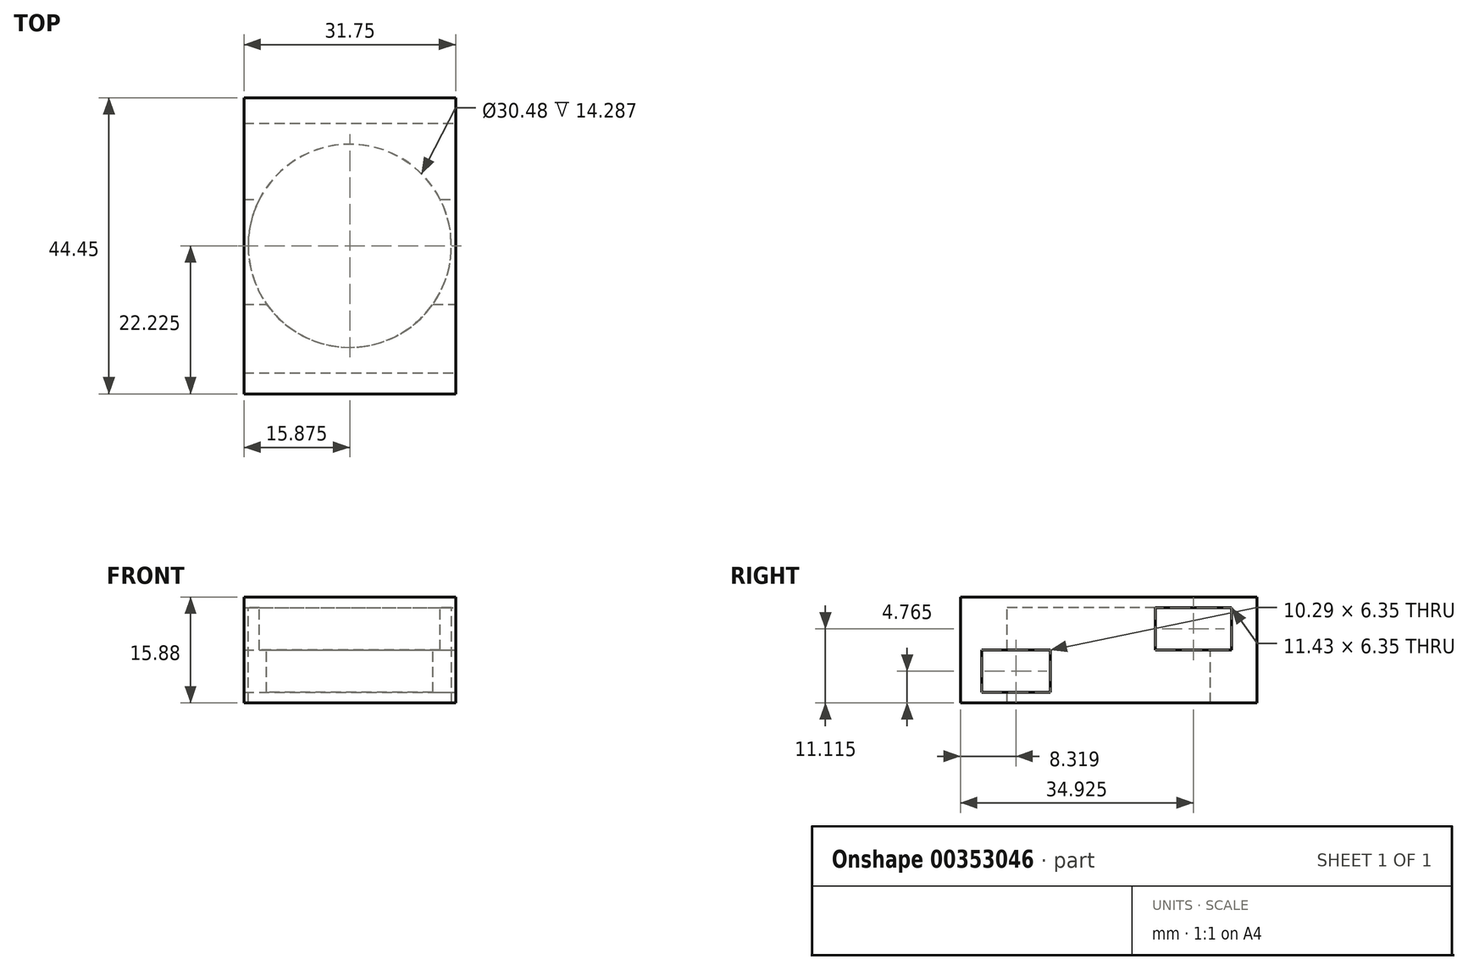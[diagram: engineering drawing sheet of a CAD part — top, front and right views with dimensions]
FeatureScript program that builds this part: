
annotation { "Feature Type Name" : "Feature", "Feature Type Description" : "" }
export const myFeature = defineFeature(function(context is Context, id is Id, definition is map)
    precondition{}
    {
        {
            var Q0;
            Q0=qCreatedBy(makeId("Top.planeOp"),FACE);
            var sketch = newSketch(context, id + "F0", { "sketchPlane" : qUnion([Q0])});
            skLineSegment(sketch, "E0.bottom", {"start": v(0, 0) * mm, "end": v(31.75, 0) * mm});
            skLineSegment(sketch, "E0.top", {"start": v(0, 44.45) * mm, "end": v(31.75, 44.45) * mm});
            skLineSegment(sketch, "E0.left", {"start": v(0, 0) * mm, "end": v(0, 44.45) * mm});
            skLineSegment(sketch, "E0.right", {"start": v(31.75, 0) * mm, "end": v(31.75, 44.45) * mm});
            skLineSegment(sketch, "E1.0", {"start": v(0, 3.81) * mm, "end": v(31.75, 3.81) * mm});
            skLineSegment(sketch, "E2.0", {"start": v(0, 40.64) * mm, "end": v(31.75, 40.64) * mm});
            skLineSegment(sketch, "E3.0", {"start": v(0, 15.24) * mm, "end": v(31.75, 15.24) * mm});
            skLineSegment(sketch, "E4.0", {"start": v(0, 29.21) * mm, "end": v(31.75, 29.21) * mm});
            skLineSegment(sketch, "E5.0", {"start": v(0, 22.23) * mm, "end": v(31.75, 22.23) * mm});
            skLineSegment(sketch, "E6.0", {"start": v(15.88, 0) * mm, "end": v(15.87, 44.45) * mm, "construction": true});
            skCircle(sketch, "E7", {"center": v(15.88, 22.23) * mm, "radius": 15.24 * mm});
            skSolve(sketch);
        }
        {
            var Q0;
            {var subQ0=sQuery(id+"F0.wireOp",EDGE,"E4.0");var subQ1=sQuery(id+"F0.wireOp",EDGE,"E0.left");var subQ2=makeQuery(id+"F0.imprint","INTERSECT",VERTEX,{"derivedFrom":[subQ1,subQ0]});Q0=makeQuery(id+"F0.imprint","IMPRINT",FACE,{"disambiguationData":[TD([[makeQuery(id+"F0.imprint","IMPRINT",EDGE,{"disambiguationData":[TD([[subQ2,1.0]])],"derivedFrom":subQ1}),-1.0]])]});}
            var Q1;
            {var subQ0=sQuery(id+"F0.wireOp",EDGE,"E3.0");var subQ1=sQuery(id+"F0.wireOp",EDGE,"E0.left");var subQ2=makeQuery(id+"F0.imprint","INTERSECT",VERTEX,{"derivedFrom":[subQ1,subQ0]});Q1=makeQuery(id+"F0.imprint","IMPRINT",FACE,{"disambiguationData":[TD([[makeQuery(id+"F0.imprint","IMPRINT",EDGE,{"disambiguationData":[TD([[subQ2,-1.0]])],"derivedFrom":subQ1}),-1.0]])]});}
            var Q2;
            {var subQ0=sQuery(id+"F0.wireOp",EDGE,"E3.0");var subQ1=sQuery(id+"F0.wireOp",EDGE,"E0.right");var subQ2=makeQuery(id+"F0.imprint","INTERSECT",VERTEX,{"derivedFrom":[subQ1,subQ0]});Q2=makeQuery(id+"F0.imprint","IMPRINT",FACE,{"disambiguationData":[TD([[makeQuery(id+"F0.imprint","IMPRINT",EDGE,{"disambiguationData":[TD([[subQ2,-1.0]])],"derivedFrom":subQ1}),1.0]])]});}
            var Q3;
            {var subQ0=sQuery(id+"F0.wireOp",EDGE,"E4.0");var subQ1=sQuery(id+"F0.wireOp",EDGE,"E0.right");var subQ2=makeQuery(id+"F0.imprint","INTERSECT",VERTEX,{"derivedFrom":[subQ1,subQ0]});Q3=makeQuery(id+"F0.imprint","IMPRINT",FACE,{"disambiguationData":[TD([[makeQuery(id+"F0.imprint","IMPRINT",EDGE,{"disambiguationData":[TD([[subQ2,1.0]])],"derivedFrom":subQ1}),1.0]])]});}
            var Q4;
            {var subQ0=sQuery(id+"F0.wireOp",EDGE,"E0.top");Q4=makeQuery(id+"F0.imprint","IMPRINT",FACE,{"disambiguationData":[TD([[makeQuery(id+"F0.imprint","IMPRINT",EDGE,{"derivedFrom":subQ0}),-1.0]])]});}
            var Q5;
            {var subQ0=sQuery(id+"F0.wireOp",EDGE,"E0.bottom");Q5=makeQuery(id+"F0.imprint","IMPRINT",FACE,{"disambiguationData":[TD([[makeQuery(id+"F0.imprint","IMPRINT",EDGE,{"derivedFrom":subQ0}),1.0]])]});}
            var Q6;
            {var subQ5=sQuery(id+"F0.wireOp",EDGE,"E2.0");Q6=makeQuery(id+"F0.imprint","IMPRINT",FACE,{"disambiguationData":[TD([[makeQuery(id+"F0.imprint","IMPRINT",EDGE,{"derivedFrom":subQ5}),-1.0]])]});}
            var Q7;
            {var subQ0=sQuery(id+"F0.wireOp",EDGE,"t68apyPM-242e-4U8n-8JZw-UtSXNeyewEgV");var subQ6=sQuery(id+"F0.wireOp",EDGE,"E3.0");var subQ7=makeQuery(id+"F0.imprint","INTERSECT",VERTEX,{"disambiguationData":[OD(0.0)],"derivedFrom":[subQ6,subQ0]});Q7=makeQuery(id+"F0.imprint","IMPRINT",FACE,{"disambiguationData":[TD([[makeQuery(id+"F0.imprint","IMPRINT",EDGE,{"disambiguationData":[TD([[subQ7,-1.0]])],"derivedFrom":subQ6}),1.0]])]});}
            var Q8;
            {var subQ0=sQuery(id+"F0.wireOp",EDGE,"t68apyPM-242e-4U8n-8JZw-UtSXNeyewEgV");var subQ1=sQuery(id+"F0.wireOp",EDGE,"E4.0");var subQ2=makeQuery(id+"F0.imprint","INTERSECT",VERTEX,{"disambiguationData":[OD(0.0)],"derivedFrom":[subQ1,subQ0]});Q8=makeQuery(id+"F0.imprint","IMPRINT",FACE,{"disambiguationData":[TD([[makeQuery(id+"F0.imprint","IMPRINT",EDGE,{"disambiguationData":[TD([[subQ2,-1.0]])],"derivedFrom":subQ1}),1.0]])]});}
            var Q9;
            {var subQ0=sQuery(id+"F0.wireOp",EDGE,"t68apyPM-242e-4U8n-8JZw-UtSXNeyewEgV");var subQ1=sQuery(id+"F0.wireOp",EDGE,"E3.0");var subQ2=makeQuery(id+"F0.imprint","INTERSECT",VERTEX,{"disambiguationData":[OD(0.0)],"derivedFrom":[subQ1,subQ0]});Q9=makeQuery(id+"F0.imprint","IMPRINT",FACE,{"disambiguationData":[TD([[makeQuery(id+"F0.imprint","IMPRINT",EDGE,{"disambiguationData":[TD([[subQ2,-1.0]])],"derivedFrom":subQ1}),-1.0]])]});}
            var Q10;
            {var subQ5=sQuery(id+"F0.wireOp",EDGE,"E1.0");Q10=makeQuery(id+"F0.imprint","IMPRINT",FACE,{"disambiguationData":[TD([[makeQuery(id+"F0.imprint","IMPRINT",EDGE,{"derivedFrom":subQ5}),1.0]])]});}
            var Q11;
            {var subQ4=sQuery(id+"F0.wireOp",EDGE,"875f277c-4cc5-4194-8c82-3089a014eff8.0");Q11=makeQuery(id+"F0.imprint","IMPRINT",FACE,{"disambiguationData":[TD([[makeQuery(id+"F0.imprint","IMPRINT",EDGE,{"derivedFrom":subQ4}),1.0]])]});}
            var Q12;
            {var subQ0=sQuery(id+"F0.wireOp",EDGE,"E7");var subQ6=sQuery(id+"F0.wireOp",EDGE,"E3.0");var subQ7=makeQuery(id+"F0.imprint","INTERSECT",VERTEX,{"disambiguationData":[OD(0.0)],"derivedFrom":[subQ6,subQ0]});Q12=makeQuery(id+"F0.imprint","IMPRINT",FACE,{"disambiguationData":[TD([[makeQuery(id+"F0.imprint","IMPRINT",EDGE,{"disambiguationData":[TD([[subQ7,-1.0]])],"derivedFrom":subQ6}),1.0]])]});}
            var Q13;
            {var subQ0=sQuery(id+"F0.wireOp",EDGE,"E7");var subQ1=sQuery(id+"F0.wireOp",EDGE,"E3.0");var subQ2=makeQuery(id+"F0.imprint","INTERSECT",VERTEX,{"disambiguationData":[OD(0.0)],"derivedFrom":[subQ1,subQ0]});Q13=makeQuery(id+"F0.imprint","IMPRINT",FACE,{"disambiguationData":[TD([[makeQuery(id+"F0.imprint","IMPRINT",EDGE,{"disambiguationData":[TD([[subQ2,-1.0]])],"derivedFrom":subQ1}),-1.0]])]});}
            var Q14;
            {var subQ0=sQuery(id+"F0.wireOp",EDGE,"E7");var subQ1=sQuery(id+"F0.wireOp",EDGE,"E4.0");var subQ2=makeQuery(id+"F0.imprint","INTERSECT",VERTEX,{"disambiguationData":[OD(0.0)],"derivedFrom":[subQ1,subQ0]});Q14=makeQuery(id+"F0.imprint","IMPRINT",FACE,{"disambiguationData":[TD([[makeQuery(id+"F0.imprint","IMPRINT",EDGE,{"disambiguationData":[TD([[subQ2,-1.0]])],"derivedFrom":subQ1}),1.0]])]});}
            var Q15;
            {var subQ0=sQuery(id+"F0.wireOp",EDGE,"E7");var subQ1=sQuery(id+"F0.wireOp",EDGE,"E4.0");var subQ2=makeQuery(id+"F0.imprint","INTERSECT",VERTEX,{"disambiguationData":[OD(0.0)],"derivedFrom":[subQ1,subQ0]});Q15=makeQuery(id+"F0.imprint","IMPRINT",FACE,{"disambiguationData":[TD([[makeQuery(id+"F0.imprint","IMPRINT",EDGE,{"disambiguationData":[TD([[subQ2,-1.0]])],"derivedFrom":subQ1}),-1.0]])]});}
            var Q16;
            Q16=sQuery(id+"F0.wireOp",EDGE,"t68apyPM-242e-4U8n-8JZw-UtSXNeyewEgV");
            extrude(context, id + "F1", {"entities" : qUnion([Q0, Q1, Q2, Q3, Q4, Q5, Q6, Q7, Q8, Q9, Q10, Q11, Q12, Q13, Q14, Q15]), "surfaceEntities" : qUnion([Q16]), "depth" : 1.59 * mm});
        }
        {
            var Q0;
            {var subQ0=sQuery(id+"F0.wireOp",EDGE,"E0.bottom");Q0=makeQuery(id+"F0.imprint","IMPRINT",FACE,{"disambiguationData":[TD([[makeQuery(id+"F0.imprint","IMPRINT",EDGE,{"derivedFrom":subQ0}),1.0]])]});}
            var Q1;
            {var subQ5=sQuery(id+"F0.wireOp",EDGE,"E1.0");Q1=makeQuery(id+"F0.imprint","IMPRINT",FACE,{"disambiguationData":[TD([[makeQuery(id+"F0.imprint","IMPRINT",EDGE,{"derivedFrom":subQ5}),1.0]])]});}
            var Q2;
            {var subQ0=sQuery(id+"F0.wireOp",EDGE,"E3.0");var subQ1=sQuery(id+"F0.wireOp",EDGE,"E0.left");var subQ2=makeQuery(id+"F0.imprint","INTERSECT",VERTEX,{"derivedFrom":[subQ1,subQ0]});Q2=makeQuery(id+"F0.imprint","IMPRINT",FACE,{"disambiguationData":[TD([[makeQuery(id+"F0.imprint","IMPRINT",EDGE,{"disambiguationData":[TD([[subQ2,-1.0]])],"derivedFrom":subQ1}),-1.0]])]});}
            var Q3;
            {var subQ0=sQuery(id+"F0.wireOp",EDGE,"E4.0");var subQ1=sQuery(id+"F0.wireOp",EDGE,"E0.left");var subQ2=makeQuery(id+"F0.imprint","INTERSECT",VERTEX,{"derivedFrom":[subQ1,subQ0]});Q3=makeQuery(id+"F0.imprint","IMPRINT",FACE,{"disambiguationData":[TD([[makeQuery(id+"F0.imprint","IMPRINT",EDGE,{"disambiguationData":[TD([[subQ2,1.0]])],"derivedFrom":subQ1}),-1.0]])]});}
            var Q4;
            {var subQ0=sQuery(id+"F0.wireOp",EDGE,"E3.0");var subQ1=sQuery(id+"F0.wireOp",EDGE,"E0.right");var subQ2=makeQuery(id+"F0.imprint","INTERSECT",VERTEX,{"derivedFrom":[subQ1,subQ0]});Q4=makeQuery(id+"F0.imprint","IMPRINT",FACE,{"disambiguationData":[TD([[makeQuery(id+"F0.imprint","IMPRINT",EDGE,{"disambiguationData":[TD([[subQ2,-1.0]])],"derivedFrom":subQ1}),1.0]])]});}
            var Q5;
            {var subQ0=sQuery(id+"F0.wireOp",EDGE,"E4.0");var subQ1=sQuery(id+"F0.wireOp",EDGE,"E0.right");var subQ2=makeQuery(id+"F0.imprint","INTERSECT",VERTEX,{"derivedFrom":[subQ1,subQ0]});Q5=makeQuery(id+"F0.imprint","IMPRINT",FACE,{"disambiguationData":[TD([[makeQuery(id+"F0.imprint","IMPRINT",EDGE,{"disambiguationData":[TD([[subQ2,1.0]])],"derivedFrom":subQ1}),1.0]])]});}
            var Q6;
            {var subQ0=sQuery(id+"F0.wireOp",EDGE,"E0.top");Q6=makeQuery(id+"F0.imprint","IMPRINT",FACE,{"disambiguationData":[TD([[makeQuery(id+"F0.imprint","IMPRINT",EDGE,{"derivedFrom":subQ0}),-1.0]])]});}
            extrude(context, id + "F2", {"entities" : qUnion([Q0, Q1, Q2, Q3, Q4, Q5, Q6]), "operationType" : NewBodyOperationType.ADD, "oppositeDirection" : true, "depth" : 6.35 * mm});
        }
        {
            var Q0;
            Q0=makeQuery(id+"F2.opExtrude","CAP_FACE",FACE,{"disambiguationData":[OSD([sQuery(id+"F0.wireOp",EDGE,"E0.bottom"),sQuery(id+"F0.wireOp",EDGE,"E0.left"),sQuery(id+"F0.wireOp",EDGE,"E0.right"),sQuery(id+"F0.wireOp",EDGE,"E4.0"),sQuery(id+"F0.wireOp",EDGE,"t68apyPM-242e-4U8n-8JZw-UtSXNeyewEgV")])],"isStart":false});
            var sketch = newSketch(context, id + "F3", { "sketchPlane" : qUnion([Q0])});
            skLineSegment(sketch, "E8.0", {"start": v(0, -3.18) * mm, "end": v(31.75, -3.18) * mm});
            skLineSegment(sketch, "E9.0", {"start": v(0, -13.46) * mm, "end": v(31.75, -13.46) * mm});
            skLineSegment(sketch, "E10.bottom", {"start": v(0, -29.21) * mm, "end": v(31.75, -29.21) * mm});
            skLineSegment(sketch, "E10.top", {"start": v(0, -40.64) * mm, "end": v(31.75, -40.64) * mm});
            skLineSegment(sketch, "E10.left", {"start": v(0, -29.21) * mm, "end": v(0, -40.64) * mm});
            skLineSegment(sketch, "E10.right", {"start": v(31.75, -29.21) * mm, "end": v(31.75, -40.64) * mm});
            skSolve(sketch);
        }
        {
            var Q0;
            Q0=makeQuery(id+"F2.opExtrude","CAP_FACE",FACE,{"disambiguationData":[OSD([sQuery(id+"F0.wireOp",EDGE,"E0.top"),sQuery(id+"F0.wireOp",EDGE,"E0.left"),sQuery(id+"F0.wireOp",EDGE,"E0.right"),sQuery(id+"F0.wireOp",EDGE,"E2.0")])],"isStart":false});
            var Q1;
            {var subQ0=sQuery(id+"F3.wireOp",EDGE,"E8.0");Q1=makeQuery(id+"F3.imprint","IMPRINT",FACE,{"disambiguationData":[TD([[makeQuery(id+"F3.imprint","IMPRINT",EDGE,{"derivedFrom":subQ0}),1.0]])]});}
            var Q2;
            {var subQ1=sQuery(id+"F0.wireOp",EDGE,"E4.0");var subQ2=sQuery(id+"F0.wireOp",EDGE,"E0.left");var subQ3=makeQuery(id+"F0.imprint","INTERSECT",VERTEX,{"derivedFrom":[subQ2,subQ1]});var subQ12=makeQuery(id+"F2.opExtrude","CAP_EDGE",EDGE,{"disambiguationData":[OSD([subQ1]),TDD([makeQuery(id+"F0.imprint","IMPRINT",EDGE,{"disambiguationData":[TD([[subQ3,-1.0]])],"derivedFrom":subQ1})])],"isStart":false});Q2=makeQuery(id+"F3.imprint","IMPRINT",FACE,{"disambiguationData":[TD([[makeQuery(id+"F3.imprint","IMPRINT",EDGE,{"derivedFrom":subQ12}),1.0]])]});}
            var Q3;
            {var subQ1=sQuery(id+"F0.wireOp",EDGE,"E4.0");var subQ2=sQuery(id+"F0.wireOp",EDGE,"E0.right");var subQ3=makeQuery(id+"F0.imprint","INTERSECT",VERTEX,{"derivedFrom":[subQ2,subQ1]});var subQ12=makeQuery(id+"F2.opExtrude","CAP_EDGE",EDGE,{"disambiguationData":[OSD([subQ1]),TDD([makeQuery(id+"F0.imprint","IMPRINT",EDGE,{"disambiguationData":[TD([[subQ3,1.0]])],"derivedFrom":subQ1})])],"isStart":false});Q3=makeQuery(id+"F3.imprint","IMPRINT",FACE,{"disambiguationData":[TD([[makeQuery(id+"F3.imprint","IMPRINT",EDGE,{"derivedFrom":subQ12}),1.0]])]});}
            var Q4;
            {var subQ7=makeQuery(id+"F2.opExtrude","CAP_EDGE",EDGE,{"disambiguationData":[OSD([sQuery(id+"F0.wireOp",EDGE,"t68apyPM-242e-4U8n-8JZw-UtSXNeyewEgV")])],"isStart":false});var subQ9=sQuery(id+"F3.wireOp",EDGE,"E10.bottom");var subQ10=makeQuery(id+"F3.imprint","INTERSECT",VERTEX,{"disambiguationData":[OD(1.0)],"derivedFrom":[subQ7,subQ9]});Q4=makeQuery(id+"F3.imprint","IMPRINT",FACE,{"disambiguationData":[TD([[makeQuery(id+"F3.imprint","IMPRINT",EDGE,{"disambiguationData":[TD([[subQ10,1.0]])],"derivedFrom":subQ7}),1.0]])]});}
            var Q5;
            {var subQ7=makeQuery(id+"F2.opExtrude","CAP_EDGE",EDGE,{"disambiguationData":[OSD([sQuery(id+"F0.wireOp",EDGE,"t68apyPM-242e-4U8n-8JZw-UtSXNeyewEgV")])],"isStart":false});var subQ9=sQuery(id+"F3.wireOp",EDGE,"E10.bottom");var subQ11=makeQuery(id+"F3.imprint","INTERSECT",VERTEX,{"disambiguationData":[OD(0.0)],"derivedFrom":[subQ7,subQ9]});Q5=makeQuery(id+"F3.imprint","IMPRINT",FACE,{"disambiguationData":[TD([[makeQuery(id+"F3.imprint","IMPRINT",EDGE,{"disambiguationData":[TD([[subQ11,-1.0]])],"derivedFrom":subQ7}),1.0]])]});}
            var Q6;
            Q6=makeQuery(id+"F3.imprint","IMPRINT",FACE,{"disambiguationData":[TD([[makeQuery(id+"F3.imprint","IMPRINT",EDGE,{"derivedFrom":sQuery(id+"F3.wireOp",EDGE,"E10.top")}),1.0]])]});
            var Q7;
            {var subQ7=makeQuery(id+"F2.opExtrude","CAP_EDGE",EDGE,{"disambiguationData":[OSD([sQuery(id+"F0.wireOp",EDGE,"E7")])],"isStart":false});var subQ9=sQuery(id+"F3.wireOp",EDGE,"E10.bottom");var subQ10=makeQuery(id+"F3.imprint","INTERSECT",VERTEX,{"disambiguationData":[OD(1.0)],"derivedFrom":[subQ7,subQ9]});Q7=makeQuery(id+"F3.imprint","IMPRINT",FACE,{"disambiguationData":[TD([[makeQuery(id+"F3.imprint","IMPRINT",EDGE,{"disambiguationData":[TD([[subQ10,1.0]])],"derivedFrom":subQ7}),1.0]])]});}
            var Q8;
            {var subQ7=makeQuery(id+"F2.opExtrude","CAP_EDGE",EDGE,{"disambiguationData":[OSD([sQuery(id+"F0.wireOp",EDGE,"E7")])],"isStart":false});var subQ9=sQuery(id+"F3.wireOp",EDGE,"E10.bottom");var subQ11=makeQuery(id+"F3.imprint","INTERSECT",VERTEX,{"disambiguationData":[OD(0.0)],"derivedFrom":[subQ7,subQ9]});Q8=makeQuery(id+"F3.imprint","IMPRINT",FACE,{"disambiguationData":[TD([[makeQuery(id+"F3.imprint","IMPRINT",EDGE,{"disambiguationData":[TD([[subQ11,-1.0]])],"derivedFrom":subQ7}),1.0]])]});}
            extrude(context, id + "F4", {"entities" : qUnion([Q0, Q1, Q2, Q3, Q4, Q5, Q6, Q7, Q8]), "operationType" : NewBodyOperationType.ADD, "depth" : 6.35 * mm});
        }
        {
            var Q0;
            {var subQ0=sQuery(id+"F0.wireOp",EDGE,"E0.right");var subQ1=sQuery(id+"F0.wireOp",EDGE,"E0.left");Q0=makeQuery(id+"F4.boolean.opBoolean","MERGE",FACE,{"derivedFrom":[makeQuery(id+"F4.opExtrude","CAP_FACE",FACE,{"disambiguationData":[OSD([sQuery(id+"F0.wireOp",EDGE,"E0.top"),subQ1,subQ0,sQuery(id+"F0.wireOp",EDGE,"E2.0")])],"isStart":false}),makeQuery(id+"F4.opExtrude","CAP_FACE",FACE,{"disambiguationData":[OSD([subQ1,subQ0,sQuery(id+"F0.wireOp",EDGE,"E7"),sQuery(id+"F3.wireOp",EDGE,"E9.0"),sQuery(id+"F3.wireOp",EDGE,"E10.bottom"),sQuery(id+"F3.wireOp",EDGE,"E10.top"),sQuery(id+"F3.wireOp",EDGE,"E10.left"),sQuery(id+"F3.wireOp",EDGE,"E10.right")])],"isStart":false})]});}
            var sketch = newSketch(context, id + "F5", { "sketchPlane" : qUnion([Q0])});
            skLineSegment(sketch, "E11.bottom", {"start": v(0, -44.45) * mm, "end": v(31.75, -44.45) * mm});
            skLineSegment(sketch, "E11.top", {"start": v(0, 0) * mm, "end": v(31.75, 0) * mm});
            skLineSegment(sketch, "E11.left", {"start": v(0, -44.45) * mm, "end": v(0, 0) * mm});
            skLineSegment(sketch, "E11.right", {"start": v(31.75, -44.45) * mm, "end": v(31.75, 0) * mm});
            skSolve(sketch);
        }
        {
            var Q0;
            Q0 = qSketchRegion(id + "F5", true);
            extrude(context, id + "F6", {"entities" : qUnion([Q0]), "operationType" : NewBodyOperationType.ADD, "depth" : 1.59 * mm});
        }
        {
            var Q0;
            {var subQ0=sQuery(id+"F0.wireOp",EDGE,"E7");var subQ1=sQuery(id+"F0.wireOp",EDGE,"E3.0");var subQ2=makeQuery(id+"F0.imprint","INTERSECT",VERTEX,{"disambiguationData":[OD(0.0)],"derivedFrom":[subQ1,subQ0]});Q0=makeQuery(id+"F0.imprint","IMPRINT",FACE,{"disambiguationData":[TD([[makeQuery(id+"F0.imprint","IMPRINT",EDGE,{"disambiguationData":[TD([[subQ2,-1.0]])],"derivedFrom":subQ1}),1.0]])]});}
            var Q1;
            {var subQ0=sQuery(id+"F0.wireOp",EDGE,"E7");var subQ1=sQuery(id+"F0.wireOp",EDGE,"E4.0");var subQ2=makeQuery(id+"F0.imprint","INTERSECT",VERTEX,{"disambiguationData":[OD(0.0)],"derivedFrom":[subQ1,subQ0]});Q1=makeQuery(id+"F0.imprint","IMPRINT",FACE,{"disambiguationData":[TD([[makeQuery(id+"F0.imprint","IMPRINT",EDGE,{"disambiguationData":[TD([[subQ2,-1.0]])],"derivedFrom":subQ1}),-1.0]])]});}
            var Q2;
            {var subQ0=sQuery(id+"F0.wireOp",EDGE,"E7");var subQ1=sQuery(id+"F0.wireOp",EDGE,"E3.0");var subQ2=makeQuery(id+"F0.imprint","INTERSECT",VERTEX,{"disambiguationData":[OD(0.0)],"derivedFrom":[subQ1,subQ0]});Q2=makeQuery(id+"F0.imprint","IMPRINT",FACE,{"disambiguationData":[TD([[makeQuery(id+"F0.imprint","IMPRINT",EDGE,{"disambiguationData":[TD([[subQ2,-1.0]])],"derivedFrom":subQ1}),-1.0]])]});}
            var Q3;
            {var subQ0=sQuery(id+"F0.wireOp",EDGE,"E7");var subQ1=sQuery(id+"F0.wireOp",EDGE,"E4.0");var subQ2=makeQuery(id+"F0.imprint","INTERSECT",VERTEX,{"disambiguationData":[OD(0.0)],"derivedFrom":[subQ1,subQ0]});Q3=makeQuery(id+"F0.imprint","IMPRINT",FACE,{"disambiguationData":[TD([[makeQuery(id+"F0.imprint","IMPRINT",EDGE,{"disambiguationData":[TD([[subQ2,-1.0]])],"derivedFrom":subQ1}),1.0]])]});}
            var Q4;
            Q4=makeQuery(id+"F6.opExtrude","CAP_FACE",FACE,{"disambiguationData":[OSD([sQuery(id+"F5.wireOp",EDGE,"E11.bottom"),sQuery(id+"F5.wireOp",EDGE,"E11.top"),sQuery(id+"F5.wireOp",EDGE,"E11.left"),sQuery(id+"F5.wireOp",EDGE,"E11.right")])],"isStart":false});
            extrude(context, id + "F7", {"entities" : qUnion([Q0, Q1, Q2, Q3]), "operationType" : NewBodyOperationType.REMOVE, "endBound" : BoundingType.UP_TO_SURFACE, "oppositeDirection" : true, "endBoundEntityFace" : qUnion([Q4]), "depth" : 25.4 * mm});
        }
    });
